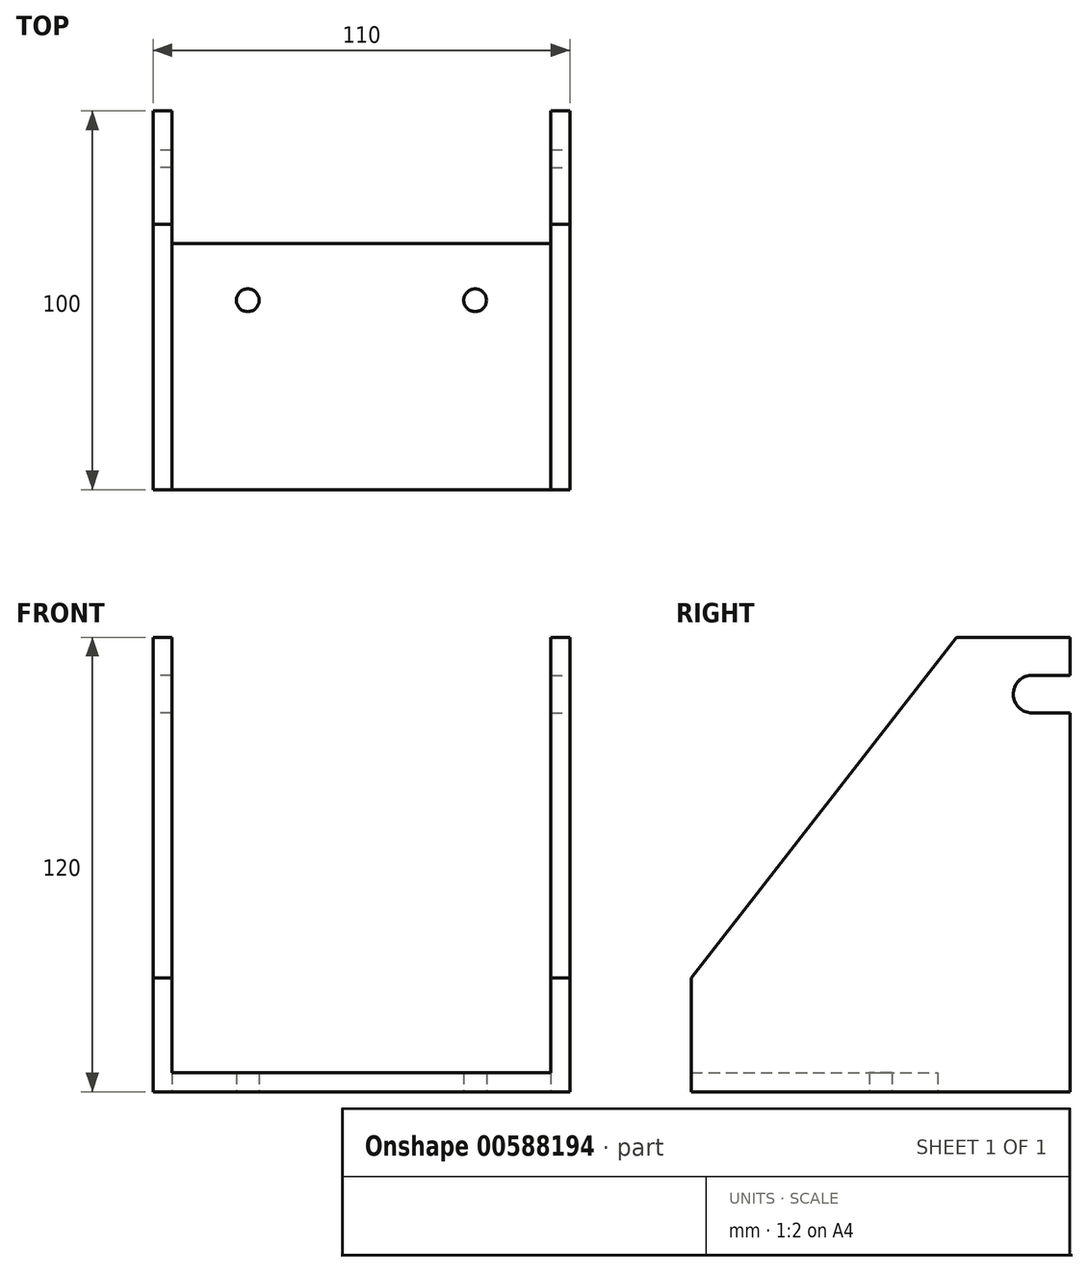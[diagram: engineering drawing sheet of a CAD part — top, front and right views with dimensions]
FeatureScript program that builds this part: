
annotation { "Feature Type Name" : "Feature", "Feature Type Description" : "" }
export const myFeature = defineFeature(function(context is Context, id is Id, definition is map)
    precondition{}
    {
        {
            var Q0;
            Q0=qCreatedBy(makeId("Top.planeOp"),FACE);
            var sketch = newSketch(context, id + "F0", { "sketchPlane" : qUnion([Q0])});
            skLineSegment(sketch, "E0.bottom", {"start": v(-74.84, -104.28) * mm, "end": v(35.16, -104.28) * mm});
            skLineSegment(sketch, "E0.top", {"start": v(-74.84, -4.28) * mm, "end": v(35.16, -4.28) * mm});
            skLineSegment(sketch, "E0.left", {"start": v(-74.84, -104.28) * mm, "end": v(-74.84, -4.28) * mm});
            skLineSegment(sketch, "E0.right", {"start": v(35.16, -104.28) * mm, "end": v(35.16, -4.28) * mm});
            skLineSegment(sketch, "E1", {"start": v(-74.84, -54.28) * mm, "end": v(35.16, -54.28) * mm, "construction": true});
            skLineSegment(sketch, "E2", {"start": v(-19.84, -4.28) * mm, "end": v(-19.84, -54.28) * mm, "construction": true});
            skLineSegment(sketch, "E3.0", {"start": v(-49.84, -4.28) * mm, "end": v(-49.84, -54.28) * mm, "construction": true});
            skLineSegment(sketch, "E4.0", {"start": v(10.16, -4.28) * mm, "end": v(10.16, -54.28) * mm, "construction": true});
            skCircle(sketch, "E5", {"center": v(-49.84, -54.28) * mm, "radius": 3 * mm});
            skCircle(sketch, "E6", {"center": v(10.16, -54.28) * mm, "radius": 3 * mm});
            skLineSegment(sketch, "E7", {"start": v(-69.84, -4.28) * mm, "end": v(-69.84, -39.28) * mm});
            skLineSegment(sketch, "E8", {"start": v(-69.84, -39.28) * mm, "end": v(30.16, -39.28) * mm});
            skLineSegment(sketch, "E9", {"start": v(30.16, -39.28) * mm, "end": v(30.16, -4.28) * mm});
            skLineSegment(sketch, "E10", {"start": v(-74.84, -9.2) * mm, "end": v(-69.84, -9.2) * mm, "construction": true});
            skLineSegment(sketch, "E11", {"start": v(30.16, -21.78) * mm, "end": v(35.16, -21.78) * mm, "construction": true});
            skPoint(sketch, "E11.endSnap0", {"position": v(30.16, -21.78) * mm});
            skSolve(sketch);
        }
        {
            var Q0;
            Q0=makeQuery(id+"F0.imprint","IMPRINT",FACE,{"disambiguationData":[TD([[makeQuery(id+"F0.imprint","IMPRINT",EDGE,{"derivedFrom":sQuery(id+"F0.wireOp",EDGE,"E0.bottom")}),1.0]])]});
            extrude(context, id + "F1", {"entities" : qUnion([Q0]), "depth" : 5 * mm, "offsetDistance" : 25 * mm});
        }
        {
            var Q0;
            Q0=makeQuery(id+"F1.opExtrude","CAP_FACE",FACE,{"disambiguationData":[OSD([sQuery(id+"F0.wireOp",EDGE,"E0.bottom"),sQuery(id+"F0.wireOp",EDGE,"E0.top"),sQuery(id+"F0.wireOp",EDGE,"E0.left"),sQuery(id+"F0.wireOp",EDGE,"E0.right")])],"isStart":false});
            var sketch = newSketch(context, id + "F2", { "sketchPlane" : qUnion([Q0])});
            skLineSegment(sketch, "E12.0", {"start": v(-69.84, -104.28) * mm, "end": v(-69.84, -4.28) * mm});
            skLineSegment(sketch, "E13.0", {"start": v(30.16, -104.28) * mm, "end": v(30.16, -4.28) * mm});
            skSolve(sketch);
        }
        {
            var Q0;
            {var subQ0=sQuery(id+"F2.wireOp",EDGE,"E12.0");Q0=makeQuery(id+"F2.imprint","IMPRINT",FACE,{"disambiguationData":[TD([[makeQuery(id+"F2.imprint","IMPRINT",EDGE,{"derivedFrom":subQ0}),1.0]])]});}
            var Q1;
            {var subQ0=sQuery(id+"F2.wireOp",EDGE,"E13.0");Q1=makeQuery(id+"F2.imprint","IMPRINT",FACE,{"disambiguationData":[TD([[makeQuery(id+"F2.imprint","IMPRINT",EDGE,{"derivedFrom":subQ0}),-1.0]])]});}
            extrude(context, id + "F3", {"entities" : qUnion([Q0, Q1]), "operationType" : NewBodyOperationType.ADD, "depth" : 115 * mm, "offsetDistance" : 25 * mm});
        }
        {
            var Q0;
            {var subQ0=sQuery(id+"F0.wireOp",EDGE,"E0.right");Q0=makeQuery(id+"F3.boolean.opBoolean","MERGE",FACE,{"derivedFrom":[makeQuery(id+"F1.opExtrude","SWEPT_FACE",FACE,{"disambiguationData":[OSD([subQ0])]}),makeQuery(id+"F3.opExtrude","SWEPT_FACE",FACE,{"disambiguationData":[OSD([subQ0])]})]});}
            var sketch = newSketch(context, id + "F4", { "sketchPlane" : qUnion([Q0])});
            skLineSegment(sketch, "E14", {"start": v(-4.28, 120) * mm, "end": v(-34.28, 120) * mm, "construction": true});
            skLineSegment(sketch, "E15", {"start": v(-104.28, 0) * mm, "end": v(-104.28, 30) * mm, "construction": true});
            skLineSegment(sketch, "E16", {"start": v(-34.28, 120) * mm, "end": v(-104.28, 30) * mm});
            skArc(sketch, "E17", {"start": v(-14.08, 110) * mm, "mid": v(-19.28, 105.1) * mm, "end": v(-14.28, 100) * mm});
            skLineSegment(sketch, "E18", {"start": v(-14.28, 105) * mm, "end": v(-14.28, 0) * mm, "construction": true});
            skLineSegment(sketch, "E19", {"start": v(-14.48, 110) * mm, "end": v(-4.28, 110) * mm});
            skLineSegment(sketch, "E20", {"start": v(-14.28, 100) * mm, "end": v(-4.28, 100) * mm});
            skSolve(sketch);
        }
        {
            var Q0;
            {var subQ0=sQuery(id+"F4.wireOp",EDGE,"E16");Q0=makeQuery(id+"F4.imprint","IMPRINT",FACE,{"disambiguationData":[TD([[makeQuery(id+"F4.imprint","IMPRINT",EDGE,{"derivedFrom":subQ0}),-1.0]])]});}
            var Q1;
            {var subQ0=sQuery(id+"F4.wireOp",EDGE,"E20");Q1=makeQuery(id+"F4.imprint","IMPRINT",FACE,{"disambiguationData":[TD([[makeQuery(id+"F4.imprint","IMPRINT",EDGE,{"derivedFrom":subQ0}),1.0]])]});}
            extrude(context, id + "F5", {"entities" : qUnion([Q0, Q1]), "operationType" : NewBodyOperationType.REMOVE, "oppositeDirection" : true, "depth" : 25 * mm, "offsetDistance" : 25 * mm});
        }
        {
            var Q0;
            {var subQ0=sQuery(id+"F0.wireOp",EDGE,"E0.left");Q0=makeQuery(id+"F3.boolean.opBoolean","MERGE",FACE,{"derivedFrom":[makeQuery(id+"F1.opExtrude","SWEPT_FACE",FACE,{"disambiguationData":[OSD([subQ0])]}),makeQuery(id+"F3.opExtrude","SWEPT_FACE",FACE,{"disambiguationData":[OSD([subQ0])]})]});}
            var sketch = newSketch(context, id + "F6", { "sketchPlane" : qUnion([Q0])});
            skLineSegment(sketch, "E21", {"start": v(104.28, 0) * mm, "end": v(104.28, 30) * mm, "construction": true});
            skLineSegment(sketch, "E22", {"start": v(4.28, 120) * mm, "end": v(34.28, 120) * mm, "construction": true});
            skLineSegment(sketch, "E23", {"start": v(34.28, 120) * mm, "end": v(104.28, 30) * mm});
            skLineSegment(sketch, "E24", {"start": v(14.28, 0) * mm, "end": v(14.28, 105) * mm, "construction": true});
            skLineSegment(sketch, "E25", {"start": v(14.28, 105) * mm, "end": v(4.28, 105) * mm, "construction": true});
            skArc(sketch, "E26", {"start": v(14.28, 100) * mm, "mid": v(19.28, 105.17) * mm, "end": v(13.95, 109.99) * mm});
            skLineSegment(sketch, "E27", {"start": v(14.61, 109.99) * mm, "end": v(4.28, 109.99) * mm});
            skLineSegment(sketch, "E28", {"start": v(14.28, 100) * mm, "end": v(4.28, 100) * mm});
            skSolve(sketch);
        }
        {
            var Q0;
            {var subQ0=sQuery(id+"F6.wireOp",EDGE,"E28");Q0=makeQuery(id+"F6.imprint","IMPRINT",FACE,{"disambiguationData":[TD([[makeQuery(id+"F6.imprint","IMPRINT",EDGE,{"derivedFrom":subQ0}),-1.0]])]});}
            var Q1;
            {var subQ0=sQuery(id+"F6.wireOp",EDGE,"E23");Q1=makeQuery(id+"F6.imprint","IMPRINT",FACE,{"disambiguationData":[TD([[makeQuery(id+"F6.imprint","IMPRINT",EDGE,{"derivedFrom":subQ0}),1.0]])]});}
            extrude(context, id + "F7", {"entities" : qUnion([Q0, Q1]), "operationType" : NewBodyOperationType.REMOVE, "oppositeDirection" : true, "depth" : 25 * mm, "offsetDistance" : 25 * mm});
        }
    });
